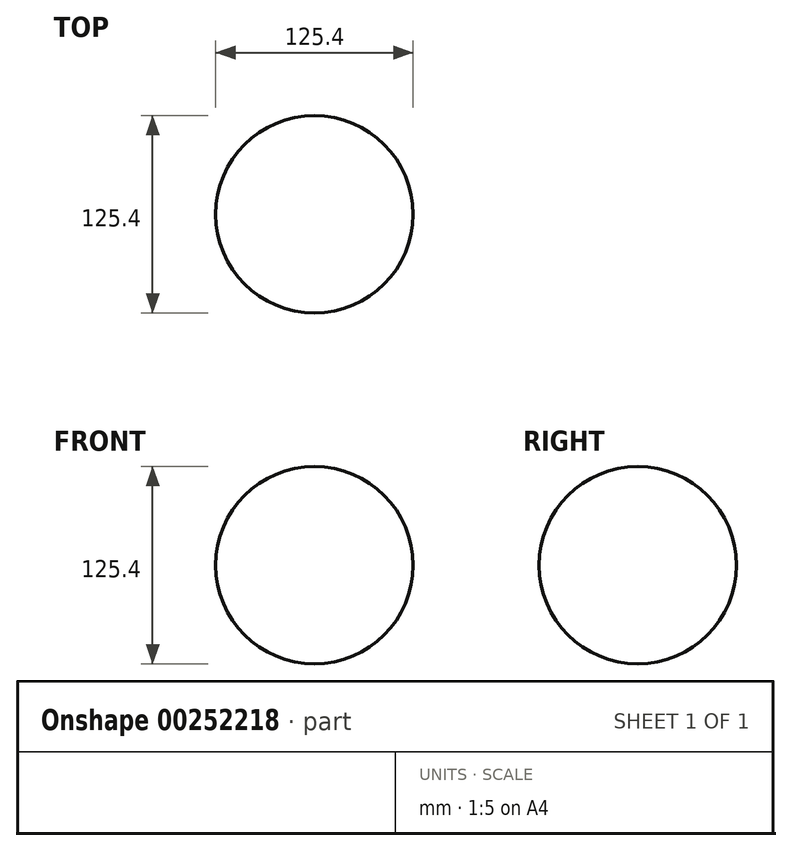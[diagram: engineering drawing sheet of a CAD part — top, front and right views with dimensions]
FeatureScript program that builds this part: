
annotation { "Feature Type Name" : "Feature", "Feature Type Description" : "" }
export const myFeature = defineFeature(function(context is Context, id is Id, definition is map)
    precondition{}
    {
        {
            var Q0;
            Q0=qCreatedBy(makeId("Front.planeOp"),FACE);
            var sketch = newSketch(context, id + "F0", { "sketchPlane" : qUnion([Q0])});
            skLineSegment(sketch, "E0", {"start": v(0, -90.86) * mm, "end": v(0, 90.86) * mm, "construction": true});
            skArc(sketch, "E1", {"start": v(0, 62.7) * mm, "mid": v(-62.7, 0) * mm, "end": v(0, -62.7) * mm});
            skLineSegment(sketch, "E2", {"start": v(0, 62.7) * mm, "end": v(0, -62.7) * mm});
            skSolve(sketch);
        }
        {
            var Q0;
            Q0=makeQuery(id+"F0.imprint","IMPRINT",FACE,{"disambiguationData":[TD([[makeQuery(id+"F0.imprint","IMPRINT",EDGE,{"derivedFrom":sQuery(id+"F0.wireOp",EDGE,"E1")}),1.0]])]});
            var Q1;
            Q1=sQuery(id+"F0.wireOp",EDGE,"E0");
            revolve(context, id + "F1", {"entities" : qUnion([Q0]), "axis" : qUnion([Q1]), "revolveType" : RevolveType.FULL});
        }
    });
